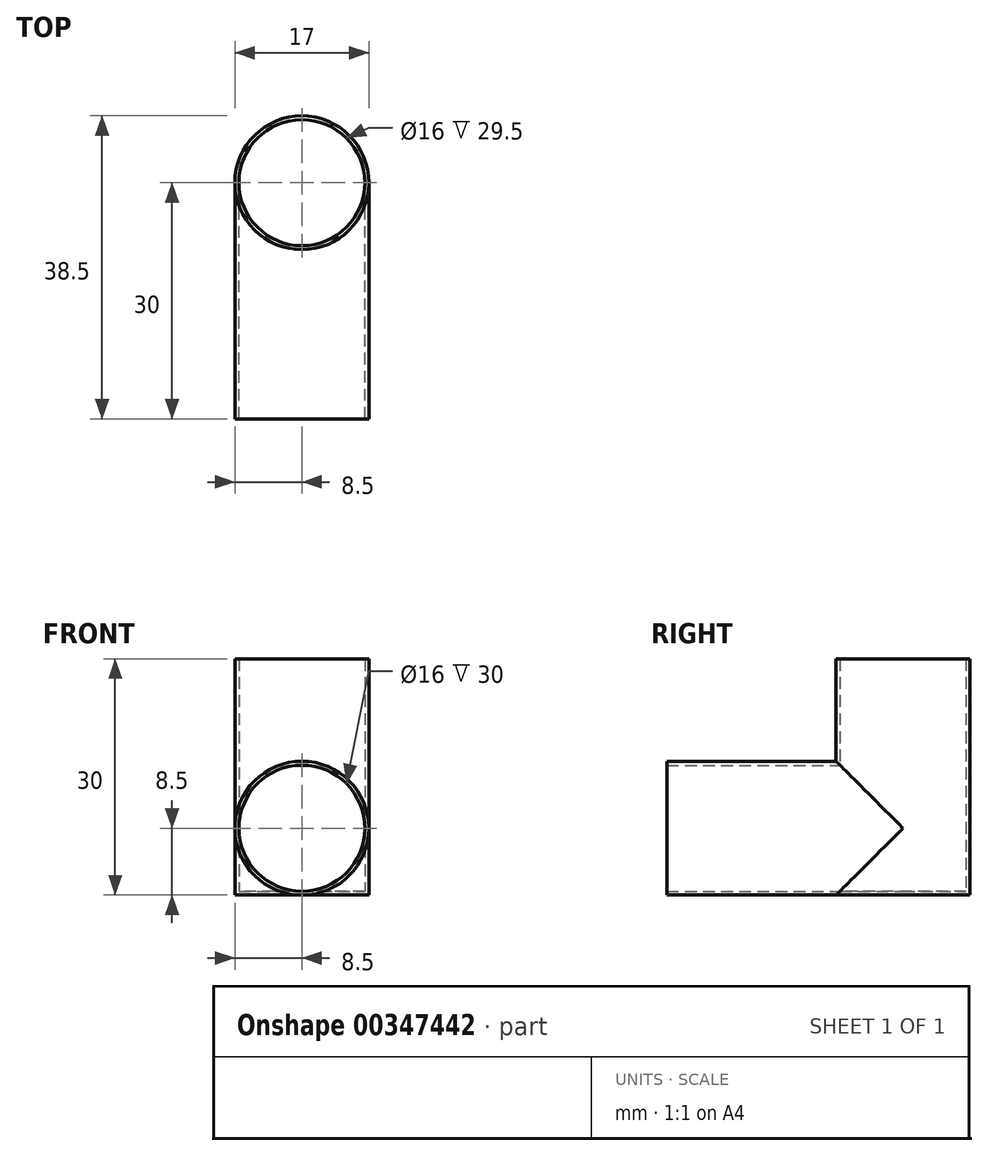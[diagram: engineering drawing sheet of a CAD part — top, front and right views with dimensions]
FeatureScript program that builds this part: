
annotation { "Feature Type Name" : "Feature", "Feature Type Description" : "" }
export const myFeature = defineFeature(function(context is Context, id is Id, definition is map)
    precondition{}
    {
        {
            var Q0;
            Q0=qCreatedBy(makeId("Top.planeOp"),FACE);
            var sketch = newSketch(context, id + "F0", { "sketchPlane" : qUnion([Q0])});
            skCircle(sketch, "E0", {"center": v(0, 0) * mm, "radius": 8.5 * mm});
            skCircle(sketch, "E1", {"center": v(0, 0) * mm, "radius": 8 * mm});
            skSolve(sketch);
        }
        {
            var Q0;
            Q0=makeQuery(id+"F0.imprint","IMPRINT",FACE,{"disambiguationData":[TD([[makeQuery(id+"F0.imprint","IMPRINT",EDGE,{"derivedFrom":sQuery(id+"F0.wireOp",EDGE,"E0")}),1.0]])]});
            extrude(context, id + "F1", {"entities" : qUnion([Q0]), "depth" : 30 * mm});
        }
        {
            var Q0;
            Q0=qCreatedBy(makeId("Front.planeOp"),FACE);
            var sketch = newSketch(context, id + "F2", { "sketchPlane" : qUnion([Q0])});
            skLineSegment(sketch, "E2", {"start": v(0, 0) * mm, "end": v(0, 8.5) * mm});
            skCircle(sketch, "E3", {"center": v(0, 8.5) * mm, "radius": 8.5 * mm});
            skCircle(sketch, "E4", {"center": v(0, 8.5) * mm, "radius": 8 * mm});
            skSolve(sketch);
        }
        {
            var Q0;
            Q0=makeQuery(id+"F2.imprint","IMPRINT",FACE,{"disambiguationData":[TD([[makeQuery(id+"F2.imprint","IMPRINT",EDGE,{"derivedFrom":sQuery(id+"F2.wireOp",EDGE,"E3")}),1.0]])]});
            extrude(context, id + "F3", {"entities" : qUnion([Q0]), "operationType" : NewBodyOperationType.ADD, "depth" : 30 * mm});
        }
        {
            var Q0;
            Q0=qCreatedBy(makeId("Top.planeOp"),FACE);
            var sketch = newSketch(context, id + "F4", { "sketchPlane" : qUnion([Q0])});
            skCircle(sketch, "E5", {"center": v(0, 0) * mm, "radius": 8 * mm});
            skSolve(sketch);
        }
        {
            var Q0;
            Q0=makeQuery(id+"F4.imprint","IMPRINT",FACE,{"disambiguationData":[TD([[makeQuery(id+"F4.imprint","IMPRINT",EDGE,{"derivedFrom":sQuery(id+"F4.wireOp",EDGE,"E5")}),1.0]])]});
            extrude(context, id + "F5", {"entities" : qUnion([Q0]), "operationType" : NewBodyOperationType.ADD, "depth" : 0.5 * mm});
        }
        {
            var Q0;
            Q0=makeQuery(id+"F1.opExtrude","CAP_FACE",FACE,{"disambiguationData":[OSD([sQuery(id+"F0.wireOp",EDGE,"E0"),sQuery(id+"F0.wireOp",EDGE,"E1")])],"isStart":false});
            var sketch = newSketch(context, id + "F6", { "sketchPlane" : qUnion([Q0])});
            skCircle(sketch, "E6", {"center": v(0, 0) * mm, "radius": 8 * mm});
            skPoint(sketch, "E7.orphan", {"position": v(-8, 0) * mm});
            skPoint(sketch, "E8.start.orphan", {"position": v(8, 0) * mm});
            skSolve(sketch);
        }
        {
            var Q0;
            Q0=makeQuery(id+"F6.imprint","IMPRINT",FACE,{"disambiguationData":[TD([[makeQuery(id+"F6.imprint","IMPRINT",EDGE,{"derivedFrom":sQuery(id+"F6.wireOp",EDGE,"E6")}),1.0]])]});
            extrude(context, id + "F7", {"entities" : qUnion([Q0]), "operationType" : NewBodyOperationType.REMOVE, "oppositeDirection" : true, "depth" : 19.5 * mm});
        }
        {
            var Q0;
            Q0=makeQuery(id+"F3.opExtrude","CAP_FACE",FACE,{"disambiguationData":[OSD([sQuery(id+"F2.wireOp",EDGE,"E3"),sQuery(id+"F2.wireOp",EDGE,"E4")])],"isStart":false});
            var sketch = newSketch(context, id + "F8", { "sketchPlane" : qUnion([Q0])});
            skCircle(sketch, "E9", {"center": v(0, 8.5) * mm, "radius": 8 * mm});
            skSolve(sketch);
        }
        {
            var Q0;
            Q0=makeQuery(id+"F8.imprint","IMPRINT",FACE,{"disambiguationData":[TD([[makeQuery(id+"F8.imprint","IMPRINT",EDGE,{"derivedFrom":sQuery(id+"F8.wireOp",EDGE,"E9")}),1.0]])]});
            extrude(context, id + "F9", {"entities" : qUnion([Q0]), "operationType" : NewBodyOperationType.REMOVE, "oppositeDirection" : true, "depth" : 20 * mm});
        }
        {
            var Q0;
            Q0=makeQuery(id+"F6.imprint","IMPRINT",FACE,{"disambiguationData":[TD([[makeQuery(id+"F6.imprint","IMPRINT",EDGE,{"derivedFrom":sQuery(id+"F6.wireOp",EDGE,"E6")}),1.0]])]});
            extrude(context, id + "F10", {"entities" : qUnion([Q0]), "operationType" : NewBodyOperationType.REMOVE, "oppositeDirection" : true, "depth" : 19.5 * mm});
        }
        {
            var Q0;
            Q0=makeQuery(id+"F6.imprint","IMPRINT",FACE,{"disambiguationData":[TD([[makeQuery(id+"F6.imprint","IMPRINT",EDGE,{"derivedFrom":sQuery(id+"F6.wireOp",EDGE,"E6")}),1.0]])]});
            extrude(context, id + "F11", {"entities" : qUnion([Q0]), "operationType" : NewBodyOperationType.REMOVE, "oppositeDirection" : true, "depth" : 29.5 * mm});
        }
        {
            var Q0;
            Q0=makeQuery(id+"F8.imprint","IMPRINT",FACE,{"disambiguationData":[TD([[makeQuery(id+"F8.imprint","IMPRINT",EDGE,{"derivedFrom":sQuery(id+"F8.wireOp",EDGE,"E9")}),1.0]])]});
            extrude(context, id + "F12", {"entities" : qUnion([Q0]), "operationType" : NewBodyOperationType.REMOVE, "oppositeDirection" : true, "depth" : 30 * mm});
        }
    });
